# Revit family: Winkel 40-5 4-Loch 45°
name_source: partatom
category: HLS-Bauteile
revit_build: Autodesk Revit 2017 (Build: 20190507_1515(x64)
units: mm (PartAtom-declared; Revit-internal decimal feet)

## family parameters
Arbeitsebenenbasiert = Ja
Beim Laden mit Abzugskörper schneiden = Nein
Bemaßung runder Anschluss = Durchmesser verwenden
Gemeinsam genutzt = Ja
Immer vertikal = Nein
Raumberechnungspunkt = Nein
Teiletyp = Normal

## types (1)
- Winkel 40-5 4-Loch 45°
    Anzahl Befestigungsloch = 4 St
    Artikelnummer = 08141000
    B = 40 mm  [stored 0.131234 ft]
    Breite Material = 40 mm
    EAN = 4250928419828
    Fabrikat = MEFA
    Firma = MEFA Befestigungs- und Montagesysteme GmbH
    Gewicht = 0.34 kg
    Gewicht pro Bauteil = 0.34 kg
    Kurztext1 = Winkel 4-Lo. C-Profil 45
    Kurztext2 = 45 ° Schenkel 116 x 116 mm
    L1 = 116 mm  [stored 0.380577 ft]
    L2 = 116 mm  [stored 0.380577 ft]
    Lochdurchmesser = 13 mm
    Länge Schenkel 1 = 116 mm  [stored 0.380577 ft]
    Länge Schenkel 2 = 116 mm  [stored 0.380577 ft]
    Material = Stahl
    Mengeneinheit = St
    Oberflaeche = galvanisch verzinkt
    Profil = C-Profil
    Profiltyp = 45
    S = 5 mm  [stored 0.0164042 ft]
    Sicherheitsfaktor = 0
    Stärke Material = 5 mm  [stored 0.0164042 ft]
    Vorgabe-Ansicht = 1219 mm
    Winkel = 45 °
    Winkel 1 = 45.00°
    max. Rohraußendurchmesser = 0 mm  [stored 0 ft]
    min. Rohraußendurchmesser = 0 mm  [stored 0 ft]
    vpe = 25 St

note: [stored X ft] marks values corroborated as IEEE doubles in the binary element streams (Revit-internal decimal feet)
